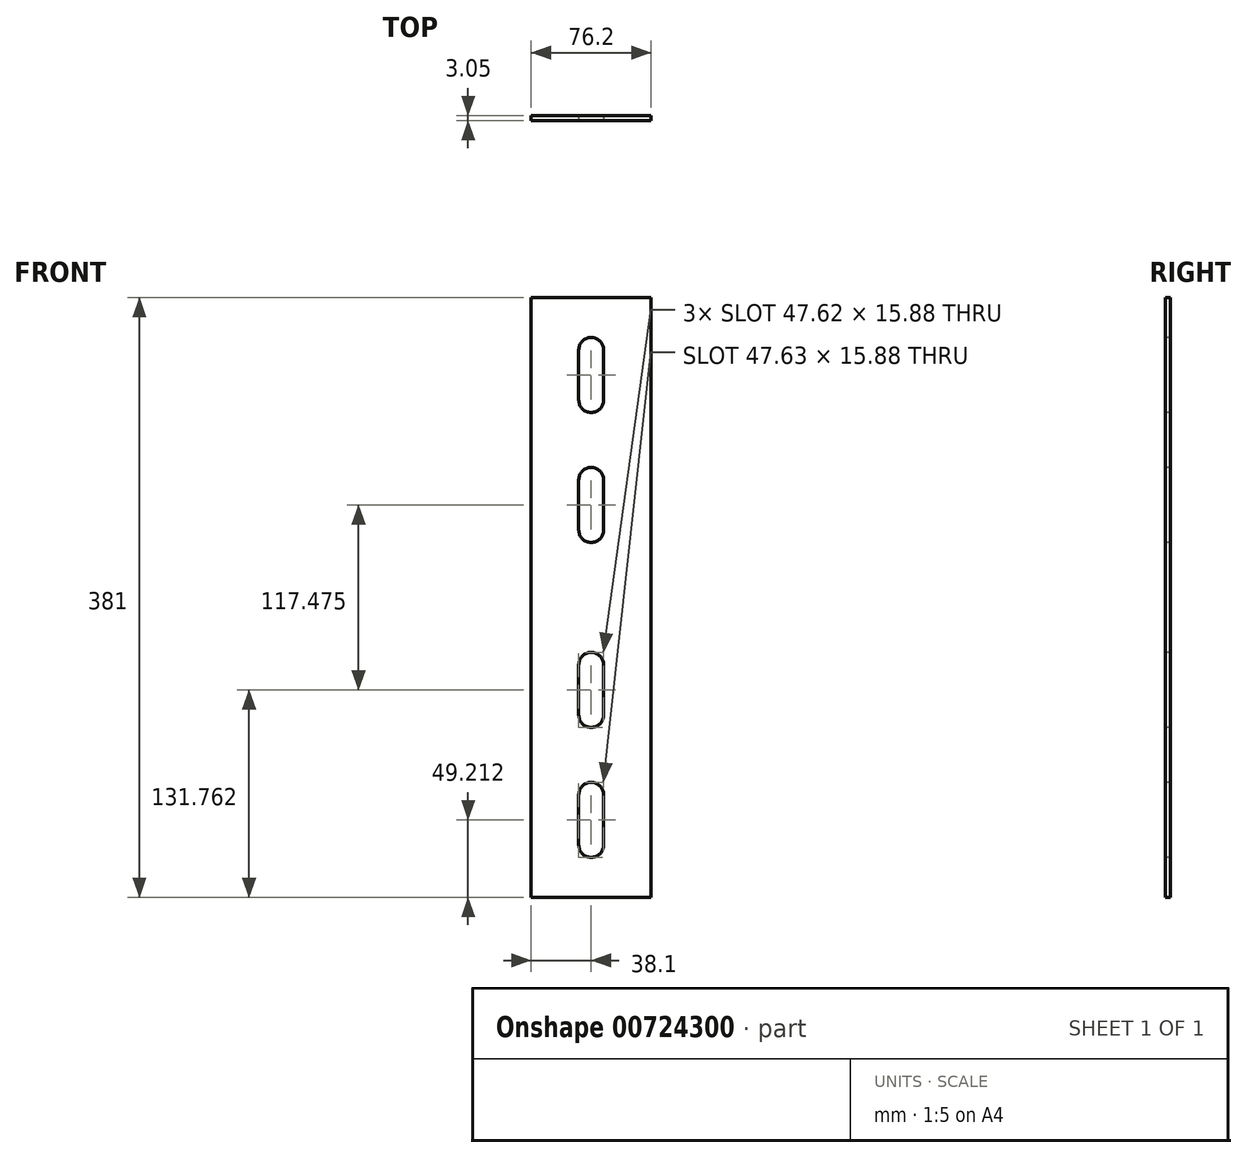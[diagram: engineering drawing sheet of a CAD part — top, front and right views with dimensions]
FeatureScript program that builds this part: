
annotation { "Feature Type Name" : "Feature", "Feature Type Description" : "" }
export const myFeature = defineFeature(function(context is Context, id is Id, definition is map)
    precondition{}
    {
        {
            var Q0;
            Q0=qCreatedBy(makeId("Top.planeOp"),FACE);
            var sketch = newSketch(context, id + "F0", { "sketchPlane" : qUnion([Q0])});
            skLineSegment(sketch, "E0.bottom", {"start": v(-38.1, -38.1) * mm, "end": v(38.1, -38.1) * mm});
            skLineSegment(sketch, "E0.left", {"start": v(-38.1, -38.1) * mm, "end": v(-38.1, 38.1) * mm});
            skLineSegment(sketch, "E0.right", {"start": v(38.1, -38.1) * mm, "end": v(38.1, 38.1) * mm});
            skPoint(sketch, "E0.middle", {"position": v(0, 0) * mm});
            skLineSegment(sketch, "E1.bottom", {"start": v(-38.1, -35.05) * mm, "end": v(38.1, -35.05) * mm});
            skSolve(sketch);
        }
        {
            var Q0;
            {var subQ2=sQuery(id+"F0.wireOp",EDGE,"E0.bottom");Q0=makeQuery(id+"F0.imprint","IMPRINT",FACE,{"disambiguationData":[TD([[makeQuery(id+"F0.imprint","IMPRINT",EDGE,{"derivedFrom":subQ2}),1.0]])]});}
            extrude(context, id + "F1", {"entities" : qUnion([Q0]), "depth" : 381 * mm, "offsetDistance" : 25.4 * mm});
        }
        {
            var Q0;
            Q0=qCreatedBy(makeId("Front.planeOp"),FACE);
            cPlane(context, id + "F2", {"entities" : qUnion([Q0]), "cplaneType" : CPlaneType.OFFSET, "offset" : 50.8 * mm, "width" : 152.4 * mm, "height" : 152.4 * mm});
        }
        {
            var Q0;
            Q0=qCreatedBy(id+"F2.planeOp",FACE);
            var sketch = newSketch(context, id + "F3", { "sketchPlane" : qUnion([Q0])});
            skLineSegment(sketch, "E2", {"start": v(-7.94, 65.09) * mm, "end": v(-7.94, 33.34) * mm});
            skLineSegment(sketch, "E3", {"start": v(7.94, 65.09) * mm, "end": v(7.94, 33.34) * mm});
            skArc(sketch, "E4", {"start": v(-7.94, 65.09) * mm, "mid": v(0, 73.03) * mm, "end": v(7.94, 65.09) * mm});
            skArc(sketch, "E5", {"start": v(-7.94, 33.34) * mm, "mid": v(0, 25.4) * mm, "end": v(7.94, 33.34) * mm});
            skLineSegment(sketch, "E6", {"start": v(-7.94, 147.64) * mm, "end": v(-7.94, 115.89) * mm});
            skLineSegment(sketch, "E7", {"start": v(7.94, 147.64) * mm, "end": v(7.94, 115.89) * mm});
            skArc(sketch, "E8", {"start": v(-7.94, 147.64) * mm, "mid": v(0, 155.58) * mm, "end": v(7.94, 147.64) * mm});
            skArc(sketch, "E9", {"start": v(-7.94, 115.89) * mm, "mid": v(0, 107.95) * mm, "end": v(7.94, 115.89) * mm});
            skLineSegment(sketch, "E10", {"start": v(-7.94, 265.11) * mm, "end": v(-7.94, 233.36) * mm});
            skLineSegment(sketch, "E11", {"start": v(7.94, 265.11) * mm, "end": v(7.94, 233.36) * mm});
            skArc(sketch, "E12", {"start": v(-7.94, 265.11) * mm, "mid": v(0, 273.05) * mm, "end": v(7.94, 265.11) * mm});
            skArc(sketch, "E13", {"start": v(-7.94, 233.36) * mm, "mid": v(0, 225.43) * mm, "end": v(7.94, 233.36) * mm});
            skLineSegment(sketch, "E14", {"start": v(-7.94, 347.66) * mm, "end": v(-7.94, 315.91) * mm});
            skLineSegment(sketch, "E15", {"start": v(7.94, 347.66) * mm, "end": v(7.94, 315.91) * mm});
            skArc(sketch, "E16", {"start": v(-7.94, 347.66) * mm, "mid": v(0, 355.6) * mm, "end": v(7.94, 347.66) * mm});
            skArc(sketch, "E17", {"start": v(-7.94, 315.91) * mm, "mid": v(0, 307.98) * mm, "end": v(7.94, 315.91) * mm});
            skSolve(sketch);
        }
        {
            var Q0;
            Q0=makeQuery(id+"F3.imprint","IMPRINT",FACE,{"disambiguationData":[TD([[makeQuery(id+"F3.imprint","IMPRINT",EDGE,{"derivedFrom":sQuery(id+"F3.wireOp",EDGE,"E6")}),1.0]])]});
            var Q1;
            Q1=makeQuery(id+"F3.imprint","IMPRINT",FACE,{"disambiguationData":[TD([[makeQuery(id+"F3.imprint","IMPRINT",EDGE,{"derivedFrom":sQuery(id+"F3.wireOp",EDGE,"E2")}),1.0]])]});
            var Q2;
            Q2=makeQuery(id+"F3.imprint","IMPRINT",FACE,{"disambiguationData":[TD([[makeQuery(id+"F3.imprint","IMPRINT",EDGE,{"derivedFrom":sQuery(id+"F3.wireOp",EDGE,"E10")}),1.0]])]});
            var Q3;
            Q3=makeQuery(id+"F3.imprint","IMPRINT",FACE,{"disambiguationData":[TD([[makeQuery(id+"F3.imprint","IMPRINT",EDGE,{"derivedFrom":sQuery(id+"F3.wireOp",EDGE,"E14")}),1.0]])]});
            extrude(context, id + "F4", {"entities" : qUnion([Q0, Q1, Q2, Q3]), "operationType" : NewBodyOperationType.REMOVE, "oppositeDirection" : true, "depth" : 25.4 * mm, "offsetDistance" : 25.4 * mm});
        }
    });
